# Revit family: 595ab18a_e3bc_4fa0_ac50_4e6f1abecd96
name_source: partatom
category: Generic Models
revit_build: Autodesk Revit Architecture 2015 (Build: 20140606_1530(x64)
units: mm (PartAtom-declared; Revit-internal decimal feet)

## types (1)
- Default
    BIMobject category = Toilets
    BOSUseNativeGeometries = 1
    Date of publishing = 7/18/2017
    Design country = Italy
    EAN code = https://8030963054897
    Edition number = 1
    IFC Classification = Sanitary Terminal
    Installation instructions = http://www.ceramicaglobo.com
    Manufacturer country = Italy
    Manufacturer name = Ceramica Globo
    Masterformat 2014 Code = 10 06 20.13
    Masterformat 2014 Description = Toilet, Bath, and Laundry Accessory Schedule
    Material main = Vitreous china
    Material secondary = Vitreous china
    NBS Reference Code = 35-65-90-97
    NBS Reference Description = Wc Systems
    Nominal height = 420
    Nominal width = 370
    OmniClass Code = 23-31 19 00
    OmniClass Description = Toilets
    Product Guid = 30d1e729-0b80-4f2f-a987-83d4861ab28a
    Product SKU = Stockholm-floor-mounted-toilet-LA001
    Product data url = https://bimobject.com
    Product family = Toilets
    Product group = Stockholm
    Product name = Stockholm floor-mounted toilet LA001
    Product url = http://www.ceramicaglobo.com
    QR code = http://bimobject.com
    Technical description = http://www.ceramicaglobo.com
    UNSPSC Code = 30181505
    Uniclass 2.0 Code = SS-35-65-90-97
    Uniclass 2.0 Description = Wc Systems
    Uniclass 2015 Code = SL_35_80_89
    Uniclass 2015 Name = Toilets
    Weight Net (Kg) = 27

## geometry (parser evidence)
native form markers: Sweep x3
no freeform markers — native parametric forms only
